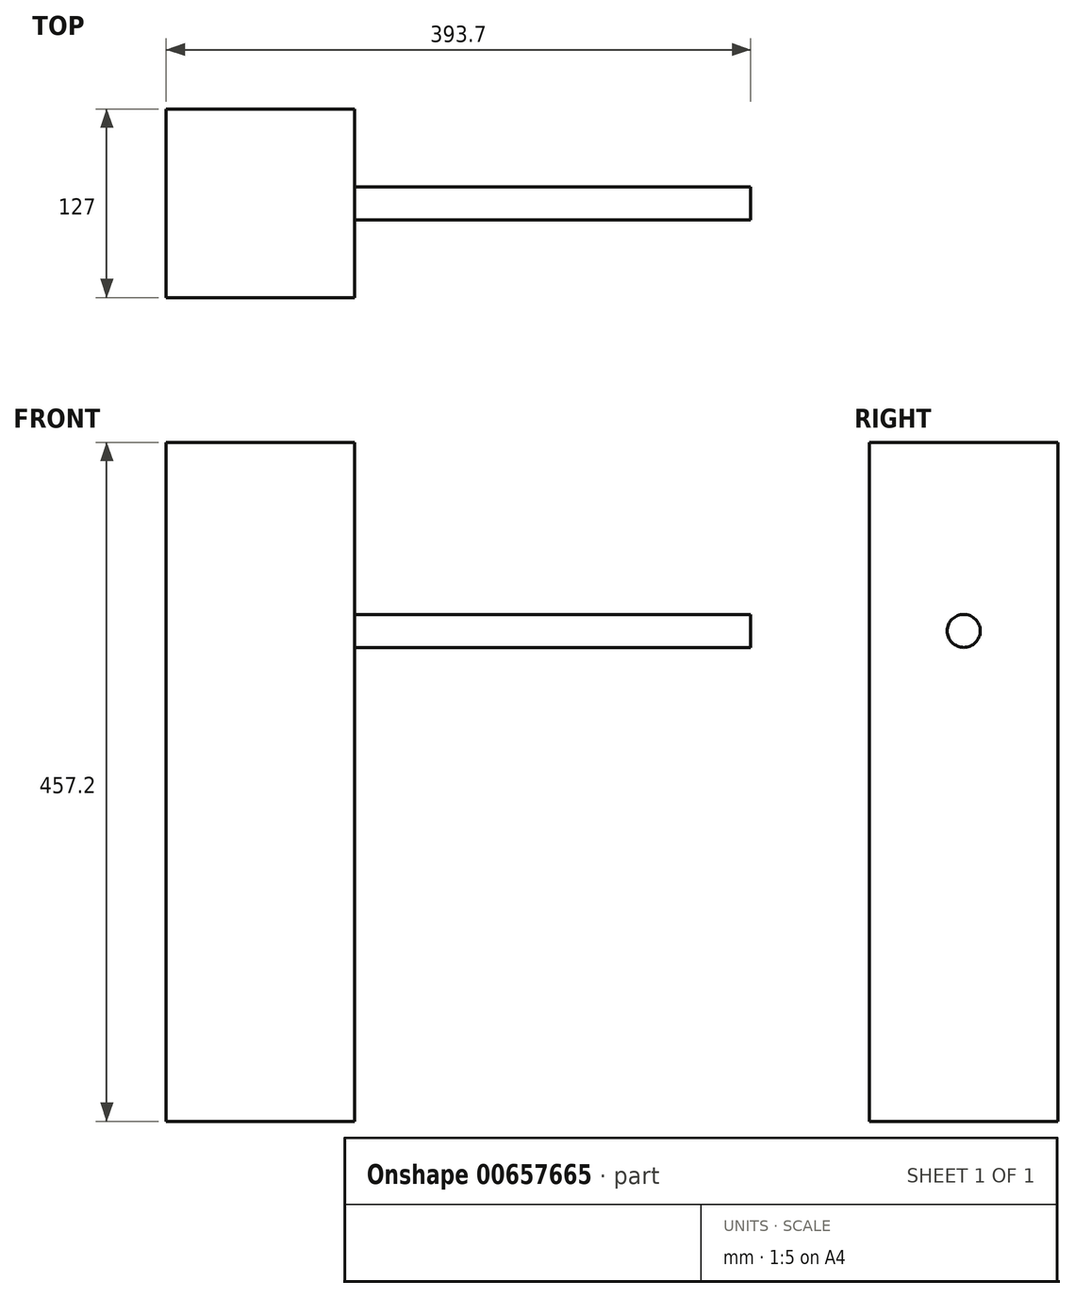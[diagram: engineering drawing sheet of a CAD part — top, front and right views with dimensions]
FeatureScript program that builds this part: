
annotation { "Feature Type Name" : "Feature", "Feature Type Description" : "" }
export const myFeature = defineFeature(function(context is Context, id is Id, definition is map)
    precondition{}
    {
        {
            var Q0;
            Q0=qCreatedBy(makeId("Top.planeOp"),FACE);
            var sketch = newSketch(context, id + "F0", { "sketchPlane" : qUnion([Q0])});
            skLineSegment(sketch, "E0.bottom", {"start": v(0, 0) * mm, "end": v(127, 0) * mm});
            skLineSegment(sketch, "E0.top", {"start": v(0, -127) * mm, "end": v(127, -127) * mm});
            skLineSegment(sketch, "E0.left", {"start": v(0, 0) * mm, "end": v(0, -127) * mm});
            skLineSegment(sketch, "E0.right", {"start": v(127, 0) * mm, "end": v(127, -127) * mm});
            skSolve(sketch);
        }
        {
            var Q0;
            Q0=makeQuery(id+"F0.imprint","IMPRINT",FACE,{"disambiguationData":[TD([[makeQuery(id+"F0.imprint","IMPRINT",EDGE,{"derivedFrom":sQuery(id+"F0.wireOp",EDGE,"E0.bottom")}),-1.0]])]});
            extrude(context, id + "F1", {"entities" : qUnion([Q0]), "depth" : 457.2 * mm, "offsetDistance" : 25.4 * mm});
        }
        {
            var Q0;
            Q0=makeQuery(id+"F1.opExtrude","SWEPT_FACE",FACE,{"disambiguationData":[OSD([sQuery(id+"F0.wireOp",EDGE,"E0.right")])]});
            var sketch = newSketch(context, id + "F2", { "sketchPlane" : qUnion([Q0])});
            skCircle(sketch, "E1", {"center": v(-63.5, 330.2) * mm, "radius": 11.11 * mm});
            skSolve(sketch);
        }
        {
            var Q0;
            Q0=makeQuery(id+"F2.imprint","IMPRINT",FACE,{"disambiguationData":[TD([[makeQuery(id+"F2.imprint","IMPRINT",EDGE,{"derivedFrom":sQuery(id+"F2.wireOp",EDGE,"ka5OggqS-vjao-uEKS-2ldV-iiNXUHrR9Vep.bottom")}),-1.0]])]});
            var Q1;
            Q1=makeQuery(id+"F2.imprint","IMPRINT",FACE,{"disambiguationData":[TD([[makeQuery(id+"F2.imprint","IMPRINT",EDGE,{"derivedFrom":sQuery(id+"F2.wireOp",EDGE,"E1")}),1.0]])]});
            extrude(context, id + "F3", {"entities" : qUnion([Q0, Q1]), "operationType" : NewBodyOperationType.ADD, "depth" : 266.7 * mm, "offsetDistance" : 25.4 * mm});
        }
    });
